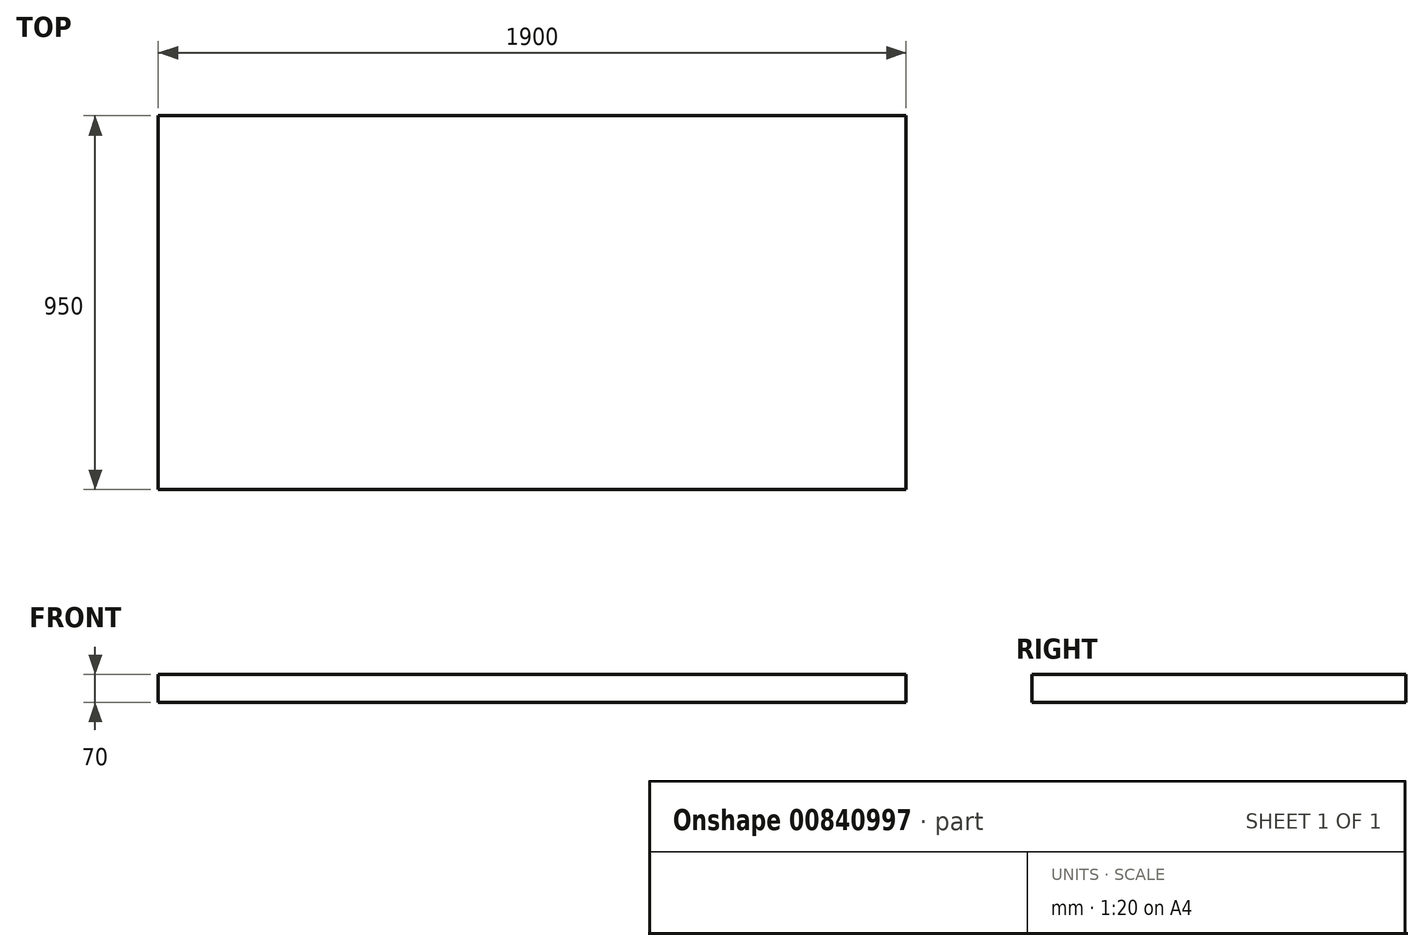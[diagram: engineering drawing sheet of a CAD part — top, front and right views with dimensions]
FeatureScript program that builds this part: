
annotation { "Feature Type Name" : "Feature", "Feature Type Description" : "" }
export const myFeature = defineFeature(function(context is Context, id is Id, definition is map)
    precondition{}
    {
        {
            var Q0;
            Q0=qCreatedBy(makeId("Top.planeOp"),FACE);
            var sketch = newSketch(context, id + "F0", { "sketchPlane" : qUnion([Q0])});
            skLineSegment(sketch, "E0.bottom", {"start": v(950, 475) * mm, "end": v(-950, 475) * mm});
            skLineSegment(sketch, "E0.top", {"start": v(950, -475) * mm, "end": v(-950, -475) * mm});
            skLineSegment(sketch, "E0.left", {"start": v(950, 475) * mm, "end": v(950, -475) * mm});
            skLineSegment(sketch, "E0.right", {"start": v(-950, 475) * mm, "end": v(-950, -475) * mm});
            skPoint(sketch, "E0.middle", {"position": v(0, 0) * mm});
            skSolve(sketch);
        }
        {
            var Q0;
            Q0 = qSketchRegion(id + "F0", true);
            extrude(context, id + "F1", {"entities" : qUnion([Q0]), "oppositeDirection" : true, "depth" : 70 * mm, "offsetDistance" : 25 * mm});
        }
    });
